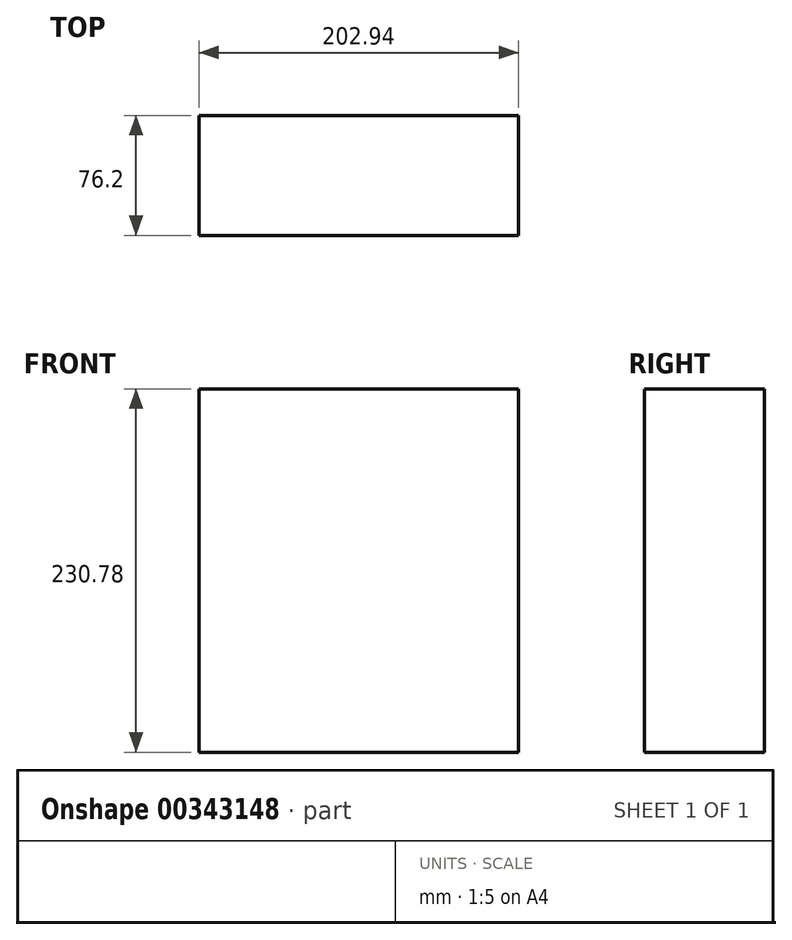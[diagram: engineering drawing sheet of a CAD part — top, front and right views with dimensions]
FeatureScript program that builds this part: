
annotation { "Feature Type Name" : "Feature", "Feature Type Description" : "" }
export const myFeature = defineFeature(function(context is Context, id is Id, definition is map)
    precondition{}
    {
        {
            var Q0;
            Q0=qCreatedBy(makeId("Front.planeOp"),FACE);
            var sketch = newSketch(context, id + "F0", { "sketchPlane" : qUnion([Q0])});
            skLineSegment(sketch, "E0.bottom", {"start": v(101.47, 115.4) * mm, "end": v(-101.47, 115.4) * mm});
            skLineSegment(sketch, "E0.top", {"start": v(101.47, -115.4) * mm, "end": v(-101.47, -115.4) * mm});
            skLineSegment(sketch, "E0.left", {"start": v(-101.47, -115.4) * mm, "end": v(-101.47, 115.4) * mm});
            skLineSegment(sketch, "E0.right", {"start": v(101.47, -115.4) * mm, "end": v(101.47, 115.4) * mm});
            skPoint(sketch, "E0.middle", {"position": v(0, 0) * mm});
            skSolve(sketch);
        }
        {
            var Q0;
            Q0=makeQuery(id+"F0.imprint","IMPRINT",FACE,{"disambiguationData":[TD([[makeQuery(id+"F0.imprint","IMPRINT",EDGE,{"derivedFrom":sQuery(id+"F0.wireOp",EDGE,"E0.bottom")}),1.0]])]});
            extrude(context, id + "F1", {"entities" : qUnion([Q0]), "depth" : 76.2 * mm});
        }
    });
